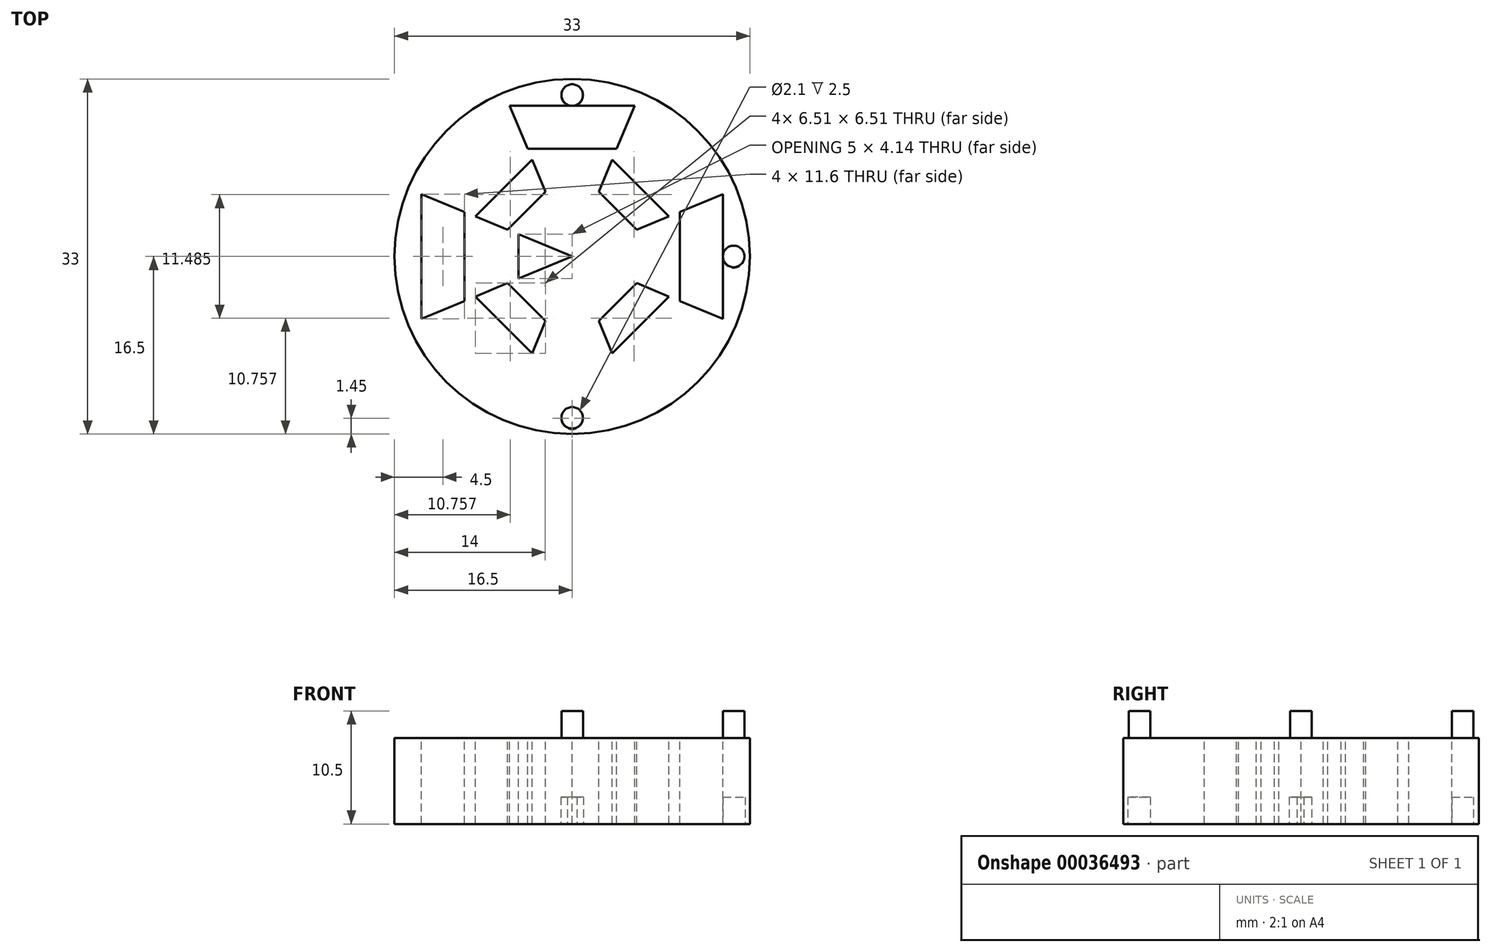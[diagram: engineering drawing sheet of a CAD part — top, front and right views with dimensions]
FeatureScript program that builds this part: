
annotation { "Feature Type Name" : "Feature", "Feature Type Description" : "" }
export const myFeature = defineFeature(function(context is Context, id is Id, definition is map)
    precondition{}
    {
        {
            var Q0;
            Q0=qCreatedBy(makeId("Top.planeOp"),FACE);
            var sketch = newSketch(context, id + "F0", { "sketchPlane" : qUnion([Q0])});
            skCircle(sketch, "E0", {"center": v(0, 0) * mm, "radius": 16.5 * mm});
            skSolve(sketch);
        }
        {
            var Q0;
            Q0=qSketchRegion(id+"F0",true);
            extrude(context, id + "F1", {"entities" : qUnion([Q0]), "depth" : 8 * mm});
        }
        {
            var Q0;
            Q0=makeQuery(id+"F1.opExtrude","CAP_FACE",FACE,{"disambiguationData":[OSD([sQuery(id+"F0.wireOp",EDGE,"E0")])],"isStart":true});
            var sketch = newSketch(context, id + "F2", { "sketchPlane" : qUnion([Q0])});
            skCircle(sketch, "E1", {"center": v(0, 15.05) * mm, "radius": 1.05 * mm});
            skCircle(sketch, "E2.1.0", {"center": v(15, 0.05) * mm, "radius": 1.05 * mm});
            skCircle(sketch, "E2.2.0", {"center": v(0, -14.95) * mm, "radius": 1.05 * mm});
            skPoint(sketch, "E2.center", {"position": v(0, 0.05) * mm});
            skLineSegment(sketch, "E2.anchor1", {"start": v(0, 0.05) * mm, "end": v(0, 15.05) * mm, "construction": true});
            skLineSegment(sketch, "E2.anchor2", {"start": v(0, 0.05) * mm, "end": v(0, -14.95) * mm, "construction": true});
            skSolve(sketch);
        }
        {
            var Q0;
            Q0=qSketchRegion(id+"F2",true);
            extrude(context, id + "F3", {"entities" : qUnion([Q0]), "operationType" : NewBodyOperationType.REMOVE, "oppositeDirection" : true, "depth" : 2.5 * mm});
        }
        {
            var Q0;
            Q0=makeQuery(id+"F1.opExtrude","CAP_FACE",FACE,{"disambiguationData":[OSD([sQuery(id+"F0.wireOp",EDGE,"E0")])],"isStart":false});
            var sketch = newSketch(context, id + "F4", { "sketchPlane" : qUnion([Q0])});
            skCircle(sketch, "E3", {"center": v(0, 15) * mm, "radius": 1 * mm});
            skCircle(sketch, "E4.1.0", {"center": v(15, 0) * mm, "radius": 1 * mm});
            skCircle(sketch, "E4.2.0", {"center": v(0, -15) * mm, "radius": 1 * mm});
            skPoint(sketch, "E4.center", {"position": v(0, 0) * mm});
            skLineSegment(sketch, "E4.anchor1", {"start": v(0, 0) * mm, "end": v(0, 15) * mm, "construction": true});
            skLineSegment(sketch, "E4.anchor2", {"start": v(0, 0) * mm, "end": v(0, -15) * mm, "construction": true});
            skSolve(sketch);
        }
        {
            var Q0;
            Q0=qSketchRegion(id+"F4",true);
            extrude(context, id + "F5", {"entities" : qUnion([Q0]), "operationType" : NewBodyOperationType.ADD, "depth" : 2.5 * mm});
        }
        {
            var Q0;
            Q0=makeQuery(id+"F1.opExtrude","CAP_FACE",FACE,{"disambiguationData":[OSD([sQuery(id+"F0.wireOp",EDGE,"E0")])],"isStart":false});
            var sketch = newSketch(context, id + "F6", { "sketchPlane" : qUnion([Q0])});
            skCircle(sketch, "E5.cCircle", {"center": v(0, 0) * mm, "radius": 14 * mm, "construction": true});
            skLineSegment(sketch, "E5.0", {"start": v(5.8, -14) * mm, "end": v(-5.8, -14) * mm});
            skLineSegment(sketch, "E5.1", {"start": v(-5.8, -14) * mm, "end": v(-14, -5.8) * mm});
            skLineSegment(sketch, "E5.2", {"start": v(-14, -5.8) * mm, "end": v(-14, 5.8) * mm});
            skLineSegment(sketch, "E5.3", {"start": v(-14, 5.8) * mm, "end": v(-5.8, 14) * mm});
            skLineSegment(sketch, "E5.4", {"start": v(-5.8, 14) * mm, "end": v(5.8, 14) * mm});
            skLineSegment(sketch, "E5.5", {"start": v(5.8, 14) * mm, "end": v(14, 5.8) * mm});
            skLineSegment(sketch, "E5.6", {"start": v(14, 5.8) * mm, "end": v(14, -5.8) * mm});
            skLineSegment(sketch, "E5.7", {"start": v(14, -5.8) * mm, "end": v(5.8, -14) * mm});
            skPoint(sketch, "E5.0.midPoint", {"position": v(0, -14) * mm});
            skCircle(sketch, "E6.cCircle", {"center": v(0, 0) * mm, "radius": 10 * mm, "construction": true});
            skLineSegment(sketch, "E6.0", {"start": v(10, -4.14) * mm, "end": v(4.14, -10) * mm});
            skLineSegment(sketch, "E6.1", {"start": v(4.14, -10) * mm, "end": v(-4.14, -10) * mm});
            skLineSegment(sketch, "E6.2", {"start": v(-4.14, -10) * mm, "end": v(-10, -4.14) * mm});
            skLineSegment(sketch, "E6.3", {"start": v(-10, -4.14) * mm, "end": v(-10, 4.14) * mm});
            skLineSegment(sketch, "E6.4", {"start": v(-10, 4.14) * mm, "end": v(-4.14, 10) * mm});
            skLineSegment(sketch, "E6.5", {"start": v(-4.14, 10) * mm, "end": v(4.14, 10) * mm});
            skLineSegment(sketch, "E6.6", {"start": v(4.14, 10) * mm, "end": v(10, 4.14) * mm});
            skLineSegment(sketch, "E6.7", {"start": v(10, 4.14) * mm, "end": v(10, -4.14) * mm});
            skPoint(sketch, "E6.0.midPoint", {"position": v(7.07, -7.07) * mm});
            skLineSegment(sketch, "E7", {"start": v(-14, 5.8) * mm, "end": v(-10, 4.14) * mm});
            skLineSegment(sketch, "E8", {"start": v(-5.8, 14) * mm, "end": v(-4.14, 10) * mm});
            skLineSegment(sketch, "E9", {"start": v(5.8, 14) * mm, "end": v(4.14, 10) * mm});
            skLineSegment(sketch, "E10", {"start": v(14, 5.8) * mm, "end": v(10, 4.14) * mm});
            skLineSegment(sketch, "E11", {"start": v(14, -5.8) * mm, "end": v(10, -4.14) * mm});
            skLineSegment(sketch, "E12", {"start": v(4.14, -10) * mm, "end": v(5.8, -14) * mm});
            skLineSegment(sketch, "E13", {"start": v(-5.8, -14) * mm, "end": v(-4.14, -10) * mm});
            skLineSegment(sketch, "E14", {"start": v(-14, -5.8) * mm, "end": v(-10, -4.14) * mm});
            skCircle(sketch, "E15.cCircle", {"center": v(0, 0) * mm, "radius": 5 * mm, "construction": true});
            skLineSegment(sketch, "E15.0", {"start": v(5, 2.07) * mm, "end": v(5, -2.07) * mm});
            skLineSegment(sketch, "E15.1", {"start": v(5, -2.07) * mm, "end": v(2.07, -5) * mm});
            skLineSegment(sketch, "E15.2", {"start": v(2.07, -5) * mm, "end": v(-2.07, -5) * mm});
            skLineSegment(sketch, "E15.3", {"start": v(-2.07, -5) * mm, "end": v(-5, -2.07) * mm});
            skLineSegment(sketch, "E15.4", {"start": v(-5, -2.07) * mm, "end": v(-5, 2.07) * mm});
            skLineSegment(sketch, "E15.5", {"start": v(-5, 2.07) * mm, "end": v(-2.07, 5) * mm});
            skLineSegment(sketch, "E15.6", {"start": v(-2.07, 5) * mm, "end": v(2.07, 5) * mm});
            skLineSegment(sketch, "E15.7", {"start": v(2.07, 5) * mm, "end": v(5, 2.07) * mm});
            skPoint(sketch, "E15.0.midPoint", {"position": v(5, 0) * mm});
            skLineSegment(sketch, "E16", {"start": v(-2.07, -5) * mm, "end": v(0, 0) * mm});
            skLineSegment(sketch, "E17", {"start": v(2.07, -5) * mm, "end": v(0, 0) * mm});
            skLineSegment(sketch, "E18", {"start": v(5, -2.07) * mm, "end": v(0, 0) * mm});
            skLineSegment(sketch, "E19", {"start": v(5, 2.07) * mm, "end": v(0, 0) * mm});
            skLineSegment(sketch, "E20", {"start": v(2.07, 5) * mm, "end": v(0, 0) * mm});
            skLineSegment(sketch, "E21", {"start": v(-2.07, 5) * mm, "end": v(0, 0) * mm});
            skLineSegment(sketch, "E22", {"start": v(-5, 2.07) * mm, "end": v(0, 0) * mm});
            skLineSegment(sketch, "E23", {"start": v(-5, -2.07) * mm, "end": v(0, 0) * mm});
            skCircle(sketch, "E24.cCircle", {"center": v(0, 0) * mm, "radius": 9 * mm, "construction": true});
            skLineSegment(sketch, "E24.0", {"start": v(9, -3.73) * mm, "end": v(3.73, -9) * mm});
            skLineSegment(sketch, "E24.1", {"start": v(3.73, -9) * mm, "end": v(-3.73, -9) * mm});
            skLineSegment(sketch, "E24.2", {"start": v(-3.73, -9) * mm, "end": v(-9, -3.73) * mm});
            skLineSegment(sketch, "E24.3", {"start": v(-9, -3.73) * mm, "end": v(-9, 3.73) * mm});
            skLineSegment(sketch, "E24.4", {"start": v(-9, 3.73) * mm, "end": v(-3.73, 9) * mm});
            skLineSegment(sketch, "E24.5", {"start": v(-3.73, 9) * mm, "end": v(3.73, 9) * mm});
            skLineSegment(sketch, "E24.6", {"start": v(3.73, 9) * mm, "end": v(9, 3.73) * mm});
            skLineSegment(sketch, "E24.7", {"start": v(9, 3.73) * mm, "end": v(9, -3.73) * mm});
            skPoint(sketch, "E24.0.midPoint", {"position": v(6.36, -6.36) * mm});
            skCircle(sketch, "E25.cCircle", {"center": v(0, 0) * mm, "radius": 6 * mm, "construction": true});
            skLineSegment(sketch, "E25.0", {"start": v(6, -2.49) * mm, "end": v(2.49, -6) * mm});
            skLineSegment(sketch, "E25.1", {"start": v(2.49, -6) * mm, "end": v(-2.49, -6) * mm});
            skLineSegment(sketch, "E25.2", {"start": v(-2.49, -6) * mm, "end": v(-6, -2.49) * mm});
            skLineSegment(sketch, "E25.3", {"start": v(-6, -2.49) * mm, "end": v(-6, 2.49) * mm});
            skLineSegment(sketch, "E25.4", {"start": v(-6, 2.49) * mm, "end": v(-2.49, 6) * mm});
            skLineSegment(sketch, "E25.5", {"start": v(-2.49, 6) * mm, "end": v(2.49, 6) * mm});
            skLineSegment(sketch, "E25.6", {"start": v(2.49, 6) * mm, "end": v(6, 2.49) * mm});
            skLineSegment(sketch, "E25.7", {"start": v(6, 2.49) * mm, "end": v(6, -2.49) * mm});
            skPoint(sketch, "E25.0.midPoint", {"position": v(4.24, -4.24) * mm});
            skLineSegment(sketch, "E26", {"start": v(-6, 2.49) * mm, "end": v(-9, 3.73) * mm});
            skLineSegment(sketch, "E27", {"start": v(-2.49, 6) * mm, "end": v(-3.73, 9) * mm});
            skLineSegment(sketch, "E28", {"start": v(2.49, 6) * mm, "end": v(3.73, 9) * mm});
            skLineSegment(sketch, "E29", {"start": v(6, 2.49) * mm, "end": v(9, 3.73) * mm});
            skLineSegment(sketch, "E30", {"start": v(6, -2.49) * mm, "end": v(9, -3.73) * mm});
            skLineSegment(sketch, "E31", {"start": v(2.49, -6) * mm, "end": v(3.73, -9) * mm});
            skLineSegment(sketch, "E32", {"start": v(-2.49, -6) * mm, "end": v(-3.73, -9) * mm});
            skLineSegment(sketch, "E33", {"start": v(-6, -2.49) * mm, "end": v(-9, -3.73) * mm});
            skSolve(sketch);
        }
        {
            var Q0;
            Q0=makeQuery(id+"F6.imprint","IMPRINT",FACE,{"disambiguationData":[TD([[makeQuery(id+"F6.imprint","IMPRINT",EDGE,{"derivedFrom":sQuery(id+"F6.wireOp",EDGE,"E5.2")}),-1.0]])]});
            var Q1;
            Q1=makeQuery(id+"F6.imprint","IMPRINT",FACE,{"disambiguationData":[TD([[makeQuery(id+"F6.imprint","IMPRINT",EDGE,{"derivedFrom":sQuery(id+"F6.wireOp",EDGE,"E6.5")}),1.0]])]});
            var Q2;
            Q2=makeQuery(id+"F6.imprint","IMPRINT",FACE,{"disambiguationData":[TD([[makeQuery(id+"F6.imprint","IMPRINT",EDGE,{"derivedFrom":sQuery(id+"F6.wireOp",EDGE,"E6.7")}),1.0]])]});
            var Q3;
            Q3=makeQuery(id+"F6.imprint","IMPRINT",FACE,{"disambiguationData":[TD([[makeQuery(id+"F6.imprint","IMPRINT",EDGE,{"derivedFrom":sQuery(id+"F6.wireOp",EDGE,"E24.2")}),-1.0]])]});
            var Q4;
            Q4=makeQuery(id+"F6.imprint","IMPRINT",FACE,{"disambiguationData":[TD([[makeQuery(id+"F6.imprint","IMPRINT",EDGE,{"derivedFrom":sQuery(id+"F6.wireOp",EDGE,"E24.0")}),-1.0]])]});
            var Q5;
            Q5=makeQuery(id+"F6.imprint","IMPRINT",FACE,{"disambiguationData":[TD([[makeQuery(id+"F6.imprint","IMPRINT",EDGE,{"derivedFrom":sQuery(id+"F6.wireOp",EDGE,"E24.4")}),-1.0]])]});
            var Q6;
            Q6=makeQuery(id+"F6.imprint","IMPRINT",FACE,{"disambiguationData":[TD([[makeQuery(id+"F6.imprint","IMPRINT",EDGE,{"derivedFrom":sQuery(id+"F6.wireOp",EDGE,"E24.6")}),-1.0]])]});
            var Q7;
            Q7=makeQuery(id+"F6.imprint","IMPRINT",FACE,{"disambiguationData":[TD([[makeQuery(id+"F6.imprint","IMPRINT",EDGE,{"derivedFrom":sQuery(id+"F6.wireOp",EDGE,"E15.4")}),-1.0]])]});
            extrude(context, id + "F7", {"entities" : qUnion([Q0, Q1, Q2, Q3, Q4, Q5, Q6, Q7]), "operationType" : NewBodyOperationType.REMOVE, "oppositeDirection" : true, "depth" : 25 * mm});
        }
    });
